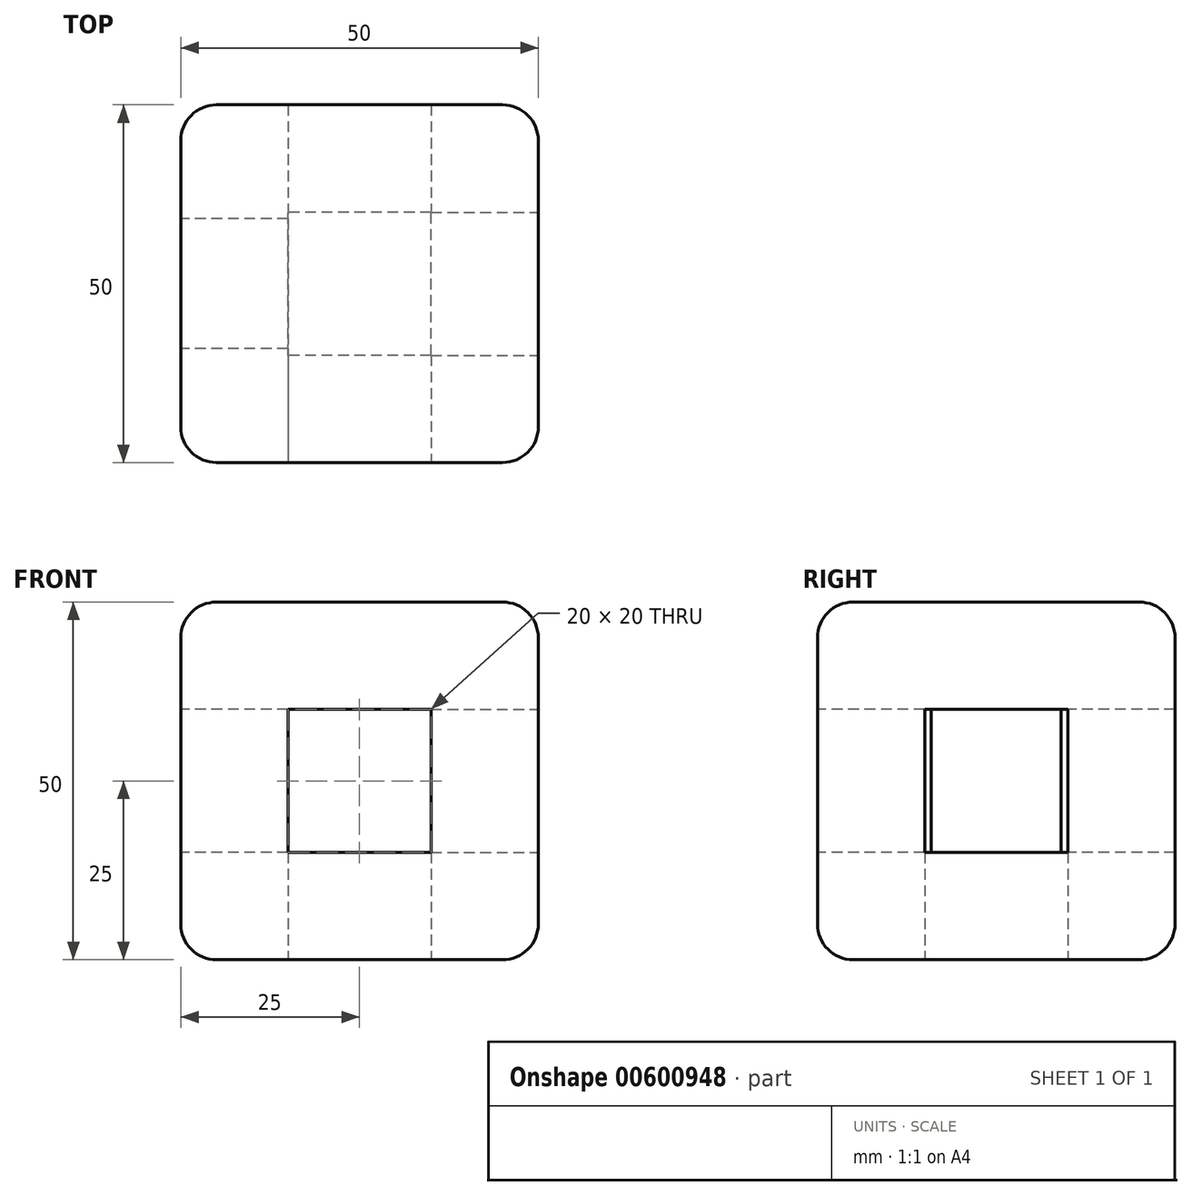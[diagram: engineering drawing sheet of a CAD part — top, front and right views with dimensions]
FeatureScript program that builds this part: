
annotation { "Feature Type Name" : "Feature", "Feature Type Description" : "" }
export const myFeature = defineFeature(function(context is Context, id is Id, definition is map)
    precondition{}
    {
        {
            var Q0;
            Q0=qCreatedBy(makeId("Front.planeOp"),FACE);
            var sketch = newSketch(context, id + "F0", { "sketchPlane" : qUnion([Q0])});
            skLineSegment(sketch, "E0.bottom", {"start": v(25, 25) * mm, "end": v(-25, 25) * mm});
            skLineSegment(sketch, "E0.top", {"start": v(25, -25) * mm, "end": v(-25, -25) * mm});
            skLineSegment(sketch, "E0.left", {"start": v(25, 25) * mm, "end": v(25, -25) * mm});
            skLineSegment(sketch, "E0.right", {"start": v(-25, 25) * mm, "end": v(-25, -25) * mm});
            skPoint(sketch, "E0.middle", {"position": v(0, 0) * mm});
            skSolve(sketch);
        }
        {
            var Q0;
            Q0 = qSketchRegion(id + "F0", true);
            extrude(context, id + "F1", {"entities" : qUnion([Q0]), "endBound" : BoundingType.SYMMETRIC, "depth" : 50 * mm, "offsetDistance" : 25 * mm});
        }
        {
            var Q0;
            Q0=makeQuery(id+"F1.opExtrude","CAP_FACE",FACE,{"disambiguationData":[OSD([sQuery(id+"F0.wireOp",EDGE,"E0.bottom"),sQuery(id+"F0.wireOp",EDGE,"E0.top"),sQuery(id+"F0.wireOp",EDGE,"E0.left"),sQuery(id+"F0.wireOp",EDGE,"E0.right")])],"isStart":false});
            var sketch = newSketch(context, id + "F2", { "sketchPlane" : qUnion([Q0])});
            skLineSegment(sketch, "E1.bottom", {"start": v(-10, 10) * mm, "end": v(10, 10) * mm});
            skLineSegment(sketch, "E1.top", {"start": v(-10, -10) * mm, "end": v(10, -10) * mm});
            skLineSegment(sketch, "E1.left", {"start": v(-10, 10) * mm, "end": v(-10, -10) * mm});
            skLineSegment(sketch, "E1.right", {"start": v(10, 10) * mm, "end": v(10, -10) * mm});
            skPoint(sketch, "E1.middle", {"position": v(0, 0) * mm});
            skSolve(sketch);
        }
        {
            var Q0;
            Q0=makeQuery(id+"F2.imprint","IMPRINT",FACE,{"disambiguationData":[TD([[makeQuery(id+"F2.imprint","IMPRINT",EDGE,{"derivedFrom":sQuery(id+"F2.wireOp",EDGE,"E1.bottom")}),-1.0]])]});
            extrude(context, id + "F3", {"entities" : qUnion([Q0]), "operationType" : NewBodyOperationType.REMOVE, "endBound" : BoundingType.UP_TO_NEXT, "oppositeDirection" : true, "depth" : 25 * mm, "offsetDistance" : 25 * mm});
        }
        {
            var Q0;
            Q0=makeQuery(id+"F1.opExtrude","SWEPT_FACE",FACE,{"disambiguationData":[OSD([sQuery(id+"F0.wireOp",EDGE,"E0.left")])]});
            var sketch = newSketch(context, id + "F4", { "sketchPlane" : qUnion([Q0])});
            skLineSegment(sketch, "E2.bottom", {"start": v(-10, -10) * mm, "end": v(10, -10) * mm});
            skLineSegment(sketch, "E2.top", {"start": v(-10, 10) * mm, "end": v(10, 10) * mm});
            skLineSegment(sketch, "E2.left", {"start": v(-10, -10) * mm, "end": v(-10, 10) * mm});
            skLineSegment(sketch, "E2.right", {"start": v(10, -10) * mm, "end": v(10, 10) * mm});
            skPoint(sketch, "E2.middle", {"position": v(0, 0) * mm});
            skSolve(sketch);
        }
        {
            var Q0;
            Q0 = qSketchRegion(id + "F4", true);
            extrude(context, id + "F5", {"entities" : qUnion([Q0]), "operationType" : NewBodyOperationType.REMOVE, "endBound" : BoundingType.UP_TO_NEXT, "oppositeDirection" : true, "depth" : 25 * mm, "offsetDistance" : 25 * mm});
        }
        {
            var Q0;
            Q0=makeQuery(id+"F1.opExtrude","SWEPT_FACE",FACE,{"disambiguationData":[OSD([sQuery(id+"F0.wireOp",EDGE,"E0.right")])]});
            var sketch = newSketch(context, id + "F6", { "sketchPlane" : qUnion([Q0])});
            skLineSegment(sketch, "E3.bottom", {"start": v(-9.1, 10) * mm, "end": v(9.1, 10) * mm});
            skLineSegment(sketch, "E3.top", {"start": v(-9.1, -10) * mm, "end": v(9.1, -10) * mm});
            skLineSegment(sketch, "E3.left", {"start": v(-9.1, 10) * mm, "end": v(-9.1, -10) * mm});
            skLineSegment(sketch, "E3.right", {"start": v(9.1, 10) * mm, "end": v(9.1, -10) * mm});
            skPoint(sketch, "E3.middle", {"position": v(0, 0) * mm});
            skSolve(sketch);
        }
        {
            var Q0;
            Q0 = qSketchRegion(id + "F6", true);
            extrude(context, id + "F7", {"entities" : qUnion([Q0]), "operationType" : NewBodyOperationType.REMOVE, "endBound" : BoundingType.UP_TO_NEXT, "oppositeDirection" : true, "depth" : 25 * mm, "offsetDistance" : 25 * mm});
        }
        {
            var Q0;
            Q0=makeQuery(id+"F1.opExtrude","CAP_EDGE",EDGE,{"disambiguationData":[OSD([sQuery(id+"F0.wireOp",EDGE,"E0.top")])],"isStart":false});
            var Q1;
            Q1=makeQuery(id+"F1.opExtrude","SWEPT_EDGE",EDGE,{"disambiguationData":[OSD([sQuery(id+"F0.wireOp",EDGE,"E0.top"),sQuery(id+"F0.wireOp",EDGE,"E0.left")])]});
            var Q2;
            Q2=makeQuery(id+"F1.opExtrude","CAP_EDGE",EDGE,{"disambiguationData":[OSD([sQuery(id+"F0.wireOp",EDGE,"E0.top")])],"isStart":true});
            var Q3;
            Q3=makeQuery(id+"F1.opExtrude","SWEPT_EDGE",EDGE,{"disambiguationData":[OSD([sQuery(id+"F0.wireOp",EDGE,"E0.top"),sQuery(id+"F0.wireOp",EDGE,"E0.right")])]});
            var Q4;
            Q4=makeQuery(id+"F1.opExtrude","CAP_EDGE",EDGE,{"disambiguationData":[OSD([sQuery(id+"F0.wireOp",EDGE,"E0.right")])],"isStart":false});
            var Q5;
            Q5=makeQuery(id+"F1.opExtrude","CAP_EDGE",EDGE,{"disambiguationData":[OSD([sQuery(id+"F0.wireOp",EDGE,"E0.right")])],"isStart":true});
            var Q6;
            Q6=makeQuery(id+"F1.opExtrude","SWEPT_EDGE",EDGE,{"disambiguationData":[OSD([sQuery(id+"F0.wireOp",EDGE,"E0.bottom"),sQuery(id+"F0.wireOp",EDGE,"E0.right")])]});
            var Q7;
            Q7=makeQuery(id+"F1.opExtrude","SWEPT_FACE",FACE,{"disambiguationData":[OSD([sQuery(id+"F0.wireOp",EDGE,"E0.bottom")])]});
            var Q8;
            Q8=makeQuery(id+"F1.opExtrude","CAP_EDGE",EDGE,{"disambiguationData":[OSD([sQuery(id+"F0.wireOp",EDGE,"E0.bottom")])],"isStart":true});
            var Q9;
            Q9=makeQuery(id+"F1.opExtrude","SWEPT_EDGE",EDGE,{"disambiguationData":[OSD([sQuery(id+"F0.wireOp",EDGE,"E0.bottom"),sQuery(id+"F0.wireOp",EDGE,"E0.left")])]});
            var Q10;
            Q10=makeQuery(id+"F1.opExtrude","CAP_EDGE",EDGE,{"disambiguationData":[OSD([sQuery(id+"F0.wireOp",EDGE,"E0.left")])],"isStart":false});
            var Q11;
            Q11=makeQuery(id+"F1.opExtrude","CAP_EDGE",EDGE,{"disambiguationData":[OSD([sQuery(id+"F0.wireOp",EDGE,"E0.left")])],"isStart":true});
            fillet(context, id + "F8", {"entities" : qUnion([Q0, Q1, Q2, Q3, Q4, Q5, Q6, Q7, Q8, Q9, Q10, Q11]), "radius" : 5 * mm, "tangentPropagation" : true, "allowEdgeOverflow" : false});
        }
        {
            var Q0;
            Q0=makeQuery(id+"F1.opExtrude","SWEPT_FACE",FACE,{"disambiguationData":[OSD([sQuery(id+"F0.wireOp",EDGE,"E0.top")])]});
            var sketch = newSketch(context, id + "F9", { "sketchPlane" : qUnion([Q0])});
            skLineSegment(sketch, "E4.bottom", {"start": v(-10, 10) * mm, "end": v(10, 10) * mm});
            skLineSegment(sketch, "E4.top", {"start": v(-10, -10) * mm, "end": v(10, -10) * mm});
            skLineSegment(sketch, "E4.left", {"start": v(-10, 10) * mm, "end": v(-10, -10) * mm});
            skLineSegment(sketch, "E4.right", {"start": v(10, 10) * mm, "end": v(10, -10) * mm});
            skPoint(sketch, "E4.middle", {"position": v(0, 0) * mm});
            skSolve(sketch);
        }
        {
            var Q0;
            Q0=makeQuery(id+"F9.imprint","IMPRINT",FACE,{"disambiguationData":[TD([[makeQuery(id+"F9.imprint","IMPRINT",EDGE,{"derivedFrom":sQuery(id+"F9.wireOp",EDGE,"E4.bottom")}),-1.0]])]});
            extrude(context, id + "F10", {"entities" : qUnion([Q0]), "operationType" : NewBodyOperationType.REMOVE, "endBound" : BoundingType.UP_TO_NEXT, "oppositeDirection" : true, "depth" : 25 * mm, "offsetDistance" : 25 * mm});
        }
    });
